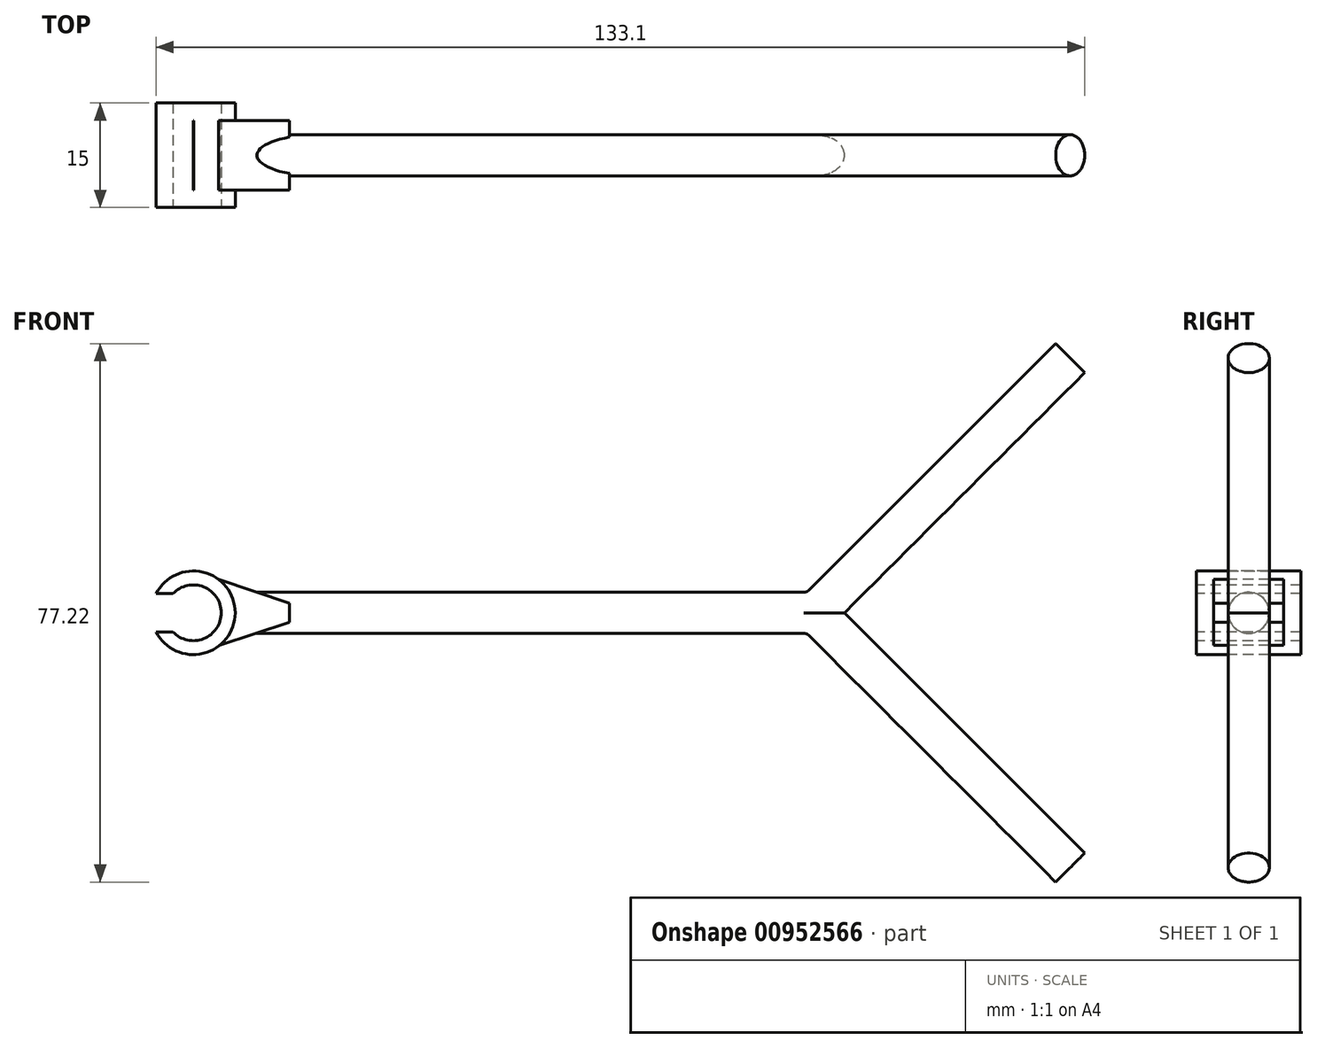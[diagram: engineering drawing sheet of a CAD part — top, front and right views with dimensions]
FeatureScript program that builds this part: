
annotation { "Feature Type Name" : "Feature", "Feature Type Description" : "" }
export const myFeature = defineFeature(function(context is Context, id is Id, definition is map)
    precondition{}
    {
        {
            var Q0;
            Q0=qCreatedBy(makeId("Front.planeOp"),FACE);
            var sketch = newSketch(context, id + "F0", { "sketchPlane" : qUnion([Q0])});
            skCircle(sketch, "E0", {"center": v(0, 0) * mm, "radius": 4 * mm});
            skCircle(sketch, "E1", {"center": v(0, 0) * mm, "radius": 6 * mm});
            skSolve(sketch);
        }
        {
            var Q0;
            Q0=qSketchRegion(id+"F0",true);
            extrude(context, id + "F1", {"entities" : qUnion([Q0]), "endBound" : BoundingType.SYMMETRIC, "oppositeDirection" : true, "depth" : 15 * mm, "offsetDistance" : 25 * mm});
        }
        {
            var Q0;
            Q0=qCreatedBy(makeId("Right.planeOp"),FACE);
            cPlane(context, id + "F2", {"entities" : qUnion([Q0]), "cplaneType" : CPlaneType.OFFSET, "offset" : 4.5 * mm, "width" : 150 * mm, "height" : 150 * mm});
        }
        {
            var Q0;
            Q0=qCreatedBy(id+"F2.planeOp",FACE);
            var sketch = newSketch(context, id + "F3", { "sketchPlane" : qUnion([Q0])});
            skCircle(sketch, "E2", {"center": v(0, 0) * mm, "radius": 2.95 * mm});
            skSolve(sketch);
        }
        {
            var Q0;
            Q0=qSketchRegion(id+"F3",true);
            extrude(context, id + "F4", {"entities" : qUnion([Q0]), "operationType" : NewBodyOperationType.ADD, "depth" : 80 * mm, "offsetDistance" : 25 * mm});
        }
        {
            var Q0;
            Q0=makeQuery(id+"F1.opExtrude","CAP_FACE",FACE,{"disambiguationData":[OSD([sQuery(id+"F0.wireOp",EDGE,"E0"),sQuery(id+"F0.wireOp",EDGE,"E1")])],"isStart":true});
            var sketch = newSketch(context, id + "F5", { "sketchPlane" : qUnion([Q0])});
            skLineSegment(sketch, "E3.bottom", {"start": v(-20, 2.75) * mm, "end": v(0, 2.75) * mm});
            skLineSegment(sketch, "E3.top", {"start": v(-20, -2.75) * mm, "end": v(0, -2.75) * mm});
            skLineSegment(sketch, "E3.left", {"start": v(-20, 2.75) * mm, "end": v(-20, -2.75) * mm});
            skLineSegment(sketch, "E3.right", {"start": v(0, 2.75) * mm, "end": v(0, -2.75) * mm});
            skPoint(sketch, "E4", {"position": v(-20, 0) * mm});
            skSolve(sketch);
        }
        {
            var Q0;
            Q0=qSketchRegion(id+"F5",true);
            extrude(context, id + "F6", {"entities" : qUnion([Q0]), "operationType" : NewBodyOperationType.REMOVE, "oppositeDirection" : true, "depth" : 25 * mm, "offsetDistance" : 25 * mm});
        }
        {
            var Q0;
            Q0=qCreatedBy(id+"F2.planeOp",FACE);
            cPlane(context, id + "F7", {"entities" : qUnion([Q0]), "cplaneType" : CPlaneType.OFFSET, "offset" : 12 * mm, "width" : 150 * mm, "height" : 150 * mm});
        }
        {
            var Q0;
            Q0=qCreatedBy(id+"F7.planeOp",FACE);
            var sketch = newSketch(context, id + "F8", { "sketchPlane" : qUnion([Q0])});
            skLineSegment(sketch, "E5", {"start": v(-2.5, 0) * mm, "end": v(2.5, 0) * mm, "construction": true});
            skPoint(sketch, "E6", {"position": v(0, 0) * mm});
            skArc(sketch, "E7", {"start": v(3.5, 0) * mm, "mid": v(2.5, 1) * mm, "end": v(1.5, 0) * mm});
            skLineSegment(sketch, "E8", {"start": v(0, 0) * mm, "end": v(0, -1.96) * mm, "construction": true});
            skArc(sketch, "E9.MirrorCS", {"start": v(-3.5, 0) * mm, "mid": v(-2.5, 1) * mm, "end": v(-1.5, 0) * mm});
            skSolve(sketch);
        }
        {
            var Q0;
            Q0=qCreatedBy(id+"F7.planeOp",FACE);
            var sketch = newSketch(context, id + "F9", { "sketchPlane" : qUnion([Q0])});
            skLineSegment(sketch, "E10", {"start": v(-4.04, 0) * mm, "end": v(4.97, 0) * mm, "construction": true});
            skSolve(sketch);
        }
        {
            var Q0;
            Q0=makeQuery(id+"F4.opExtrude","CAP_FACE",FACE,{"disambiguationData":[OSD([sQuery(id+"F3.wireOp",EDGE,"E2")])],"isStart":false});
            var sketch = newSketch(context, id + "F10", { "sketchPlane" : qUnion([Q0])});
            skCircle(sketch, "E11", {"center": v(0, 0) * mm, "radius": 2.5 * mm});
            skSolve(sketch);
        }
        {
            var Q0;
            Q0=makeQuery(id+"F0.imprint","IMPRINT",FACE,{"disambiguationData":[TD([[makeQuery(id+"F0.imprint","IMPRINT",EDGE,{"derivedFrom":sQuery(id+"F0.wireOp",EDGE,"E0")}),1.0]])]});
            var sketch = newSketch(context, id + "F11", { "sketchPlane" : qUnion([Q0])});
            skLineSegment(sketch, "E12", {"start": v(0, 6.02) * mm, "end": v(13.77, 1.37) * mm});
            skLineSegment(sketch, "E13", {"start": v(13.77, 1.37) * mm, "end": v(13.77, -1.38) * mm});
            skLineSegment(sketch, "E14", {"start": v(13.77, -1.38) * mm, "end": v(0, -5.9) * mm});
            skLineSegment(sketch, "E15", {"start": v(0, -5.9) * mm, "end": v(5.86, 0) * mm});
            skLineSegment(sketch, "E16", {"start": v(5.86, 0) * mm, "end": v(0, 6.02) * mm});
            skSolve(sketch);
        }
        {
            var Q0;
            Q0=qSketchRegion(id+"F11",true);
            extrude(context, id + "F12", {"entities" : qUnion([Q0]), "operationType" : NewBodyOperationType.ADD, "endBound" : BoundingType.SYMMETRIC, "depth" : 10 * mm, "offsetDistance" : 25 * mm});
        }
        {
            var Q0;
            Q0=qCreatedBy(makeId("Front.planeOp"),FACE);
            var sketch = newSketch(context, id + "F13", { "sketchPlane" : qUnion([Q0])});
            skLineSegment(sketch, "E17.bottom", {"start": v(79.5, 1) * mm, "end": v(76.5, 1) * mm});
            skLineSegment(sketch, "E17.top", {"start": v(79.5, -1) * mm, "end": v(76.5, -1) * mm});
            skLineSegment(sketch, "E17.left", {"start": v(79.5, 1) * mm, "end": v(79.5, -1) * mm});
            skLineSegment(sketch, "E17.right", {"start": v(76.5, 1) * mm, "end": v(76.5, -1) * mm});
            skPoint(sketch, "E18", {"position": v(79.5, 0) * mm});
            skPoint(sketch, "E19", {"position": v(84.5, 0) * mm});
            skSolve(sketch);
        }
        {
            var Q0;
            Q0=makeQuery(id+"F10.imprint","IMPRINT",FACE,{"disambiguationData":[TD([[makeQuery(id+"F10.imprint","IMPRINT",EDGE,{"derivedFrom":sQuery(id+"F10.wireOp",EDGE,"E11")}),1.0]])]});
            var sketch = newSketch(context, id + "F14", { "sketchPlane" : qUnion([Q0])});
            skCircle(sketch, "E20", {"center": v(0, 0) * mm, "radius": 2.95 * mm});
            skSolve(sketch);
        }
        {
            var Q0;
            Q0=qCreatedBy(makeId("Front.planeOp"),FACE);
            var sketch = newSketch(context, id + "F15", { "sketchPlane" : qUnion([Q0])});
            skLineSegment(sketch, "E21", {"start": v(84.5, 0) * mm, "end": v(87.5, 0) * mm});
            skLineSegment(sketch, "E22", {"start": v(91.5, -4) * mm, "end": v(91.5, -8.25) * mm, "construction": true});
            skPoint(sketch, "E23.visualSharp", {"position": v(91.5, 0) * mm});
            skArc(sketch, "E23.filletArc", {"start": v(91.5, -4) * mm, "mid": v(91.2, -2.47) * mm, "end": v(90.33, -1.17) * mm, "construction": true});
            skArc(sketch, "E24", {"start": v(90.33, -1.17) * mm, "mid": v(89.03, -0.3) * mm, "end": v(87.5, 0) * mm});
            skLineSegment(sketch, "E25", {"start": v(91.5, 0) * mm, "end": v(87.5, -4) * mm, "construction": true});
            skLineSegment(sketch, "E26", {"start": v(90.33, -1.17) * mm, "end": v(125.68, -36.53) * mm});
            skArc(sketch, "E27.MirrorCS", {"start": v(90.33, 1.17) * mm, "mid": v(89.03, 0.3) * mm, "end": v(87.5, 0) * mm});
            skLineSegment(sketch, "E28.MirrorCS", {"start": v(90.33, 1.17) * mm, "end": v(125.68, 36.53) * mm});
            skLineSegment(sketch, "E29.MirrorCS", {"start": v(91.5, 0) * mm, "end": v(87.5, 4) * mm, "construction": true});
            skLineSegment(sketch, "E30.MirrorCS", {"start": v(91.5, 4) * mm, "end": v(91.5, 8.25) * mm, "construction": true});
            skArc(sketch, "E31.MirrorCS", {"start": v(91.5, 4) * mm, "mid": v(91.2, 2.47) * mm, "end": v(90.33, 1.17) * mm, "construction": true});
            skSolve(sketch);
        }
        {
            var Q0;
            Q0=qSketchRegion(id+"F14",true);
            var Q1;
            Q1=sQuery(id+"F15.wireOp",EDGE,"E21");
            var Q2;
            Q2=sQuery(id+"F15.wireOp",EDGE,"E27.MirrorCS");
            var Q3;
            Q3=sQuery(id+"F15.wireOp",EDGE,"E28.MirrorCS");
            sweep(context, id + "F16", {"operationType" : NewBodyOperationType.ADD, "profiles" : qUnion([Q0]), "surfaceOperationType" : NewSurfaceOperationType.ADD, "path" : qUnion([Q1, Q2, Q3])});
        }
        {
            var Q0;
            Q0 = qSketchRegion(id + "F14", true);
            var Q1;
            Q1=sQuery(id+"F15.wireOp",EDGE,"E21");
            var Q2;
            Q2=sQuery(id+"F15.wireOp",EDGE,"E24");
            var Q3;
            Q3=sQuery(id+"F15.wireOp",EDGE,"E26");
            sweep(context, id + "F17", {"operationType" : NewBodyOperationType.ADD, "profiles" : qUnion([Q0]), "path" : qUnion([Q1, Q2, Q3])});
        }
    });
